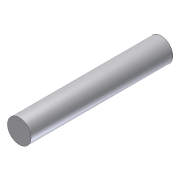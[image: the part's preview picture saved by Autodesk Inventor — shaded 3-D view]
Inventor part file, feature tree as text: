
AUTODESK INVENTOR PART (.ipt)
format: ipt  version: unknown  size: 148,480 bytes
history: native  units: in
note: dims shown in document units (in); Inventor stores cm internally (conversion verified against a paired STEP export)
features: extrude x1, sketch x1
ambient origin geometry x8: Origin, YZ Plane, XZ Plane, XY Plane, X Axis, Y Axis, Z Axis, Center Point
feature tree (2):
  extrude  "Extrusion1"  Depth=3.0in TaperAngle=0.0deg
  sketch  "Sketch1"  dims[d0=0.5in d1=3.0in d2=0.0in]
